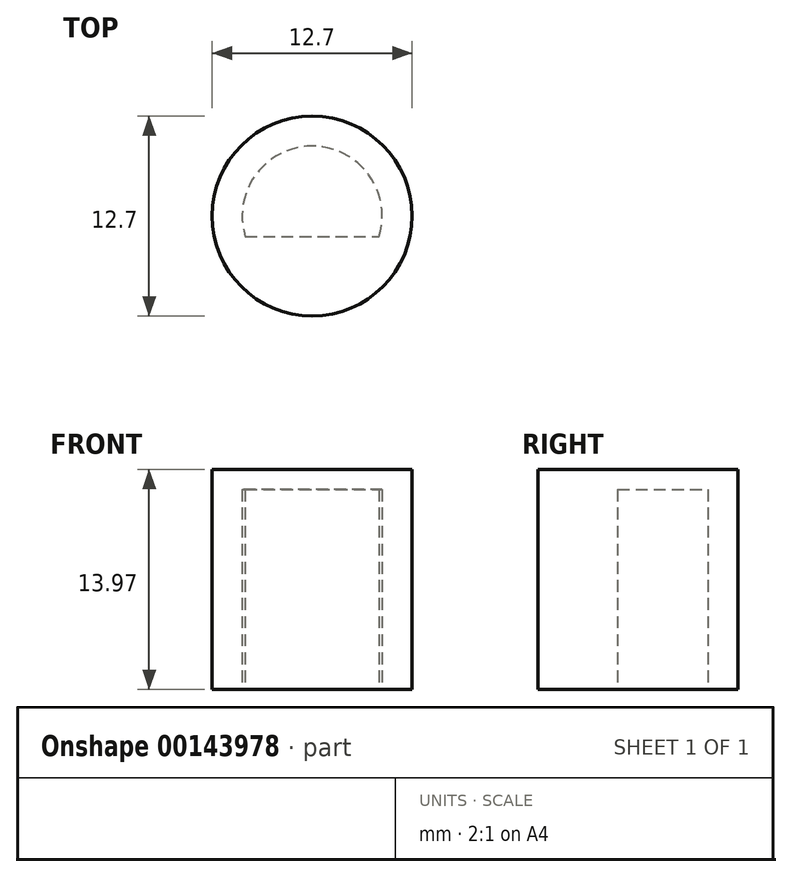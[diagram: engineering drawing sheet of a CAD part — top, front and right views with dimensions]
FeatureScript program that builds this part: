
annotation { "Feature Type Name" : "Feature", "Feature Type Description" : "" }
export const myFeature = defineFeature(function(context is Context, id is Id, definition is map)
    precondition{}
    {
        {
            var Q0;
            Q0=qCreatedBy(makeId("Top.planeOp"),FACE);
            var sketch = newSketch(context, id + "F0", { "sketchPlane" : qUnion([Q0])});
            skPoint(sketch, "E0", {"position": v(0, 0.13) * mm});
            skPoint(sketch, "E1", {"position": v(0, 4.45) * mm});
            skCircle(sketch, "E2", {"center": v(0, 0) * mm, "radius": 6.35 * mm});
            skArc(sketch, "E3", {"start": v(4.25, -1.3) * mm, "mid": v(0, 4.45) * mm, "end": v(-4.25, -1.3) * mm});
            skLineSegment(sketch, "E4", {"start": v(-4.25, -1.3) * mm, "end": v(4.25, -1.3) * mm});
            skSolve(sketch);
        }
        {
            var Q0;
            Q0=makeQuery(id+"F0.imprint","IMPRINT",FACE,{"disambiguationData":[TD([[makeQuery(id+"F0.imprint","IMPRINT",EDGE,{"derivedFrom":sQuery(id+"F0.wireOp",EDGE,"s4ZK6kcC-YwtM-Ympy-6Isc-HiUL8Dsxxq34")}),-1.0]])]});
            var Q1;
            Q1=makeQuery(id+"F0.imprint","IMPRINT",FACE,{"disambiguationData":[TD([[makeQuery(id+"F0.imprint","IMPRINT",EDGE,{"derivedFrom":sQuery(id+"F0.wireOp",EDGE,"E2")}),1.0]])]});
            extrude(context, id + "F1", {"entities" : qUnion([Q0, Q1]), "depth" : 12.7 * mm});
        }
        {
            var Q0;
            Q0=makeQuery(id+"F1.opExtrude","CAP_FACE",FACE,{"disambiguationData":[OSD([sQuery(id+"F0.wireOp",EDGE,"s4ZK6kcC-YwtM-Ympy-6Isc-HiUL8Dsxxq34"),sQuery(id+"F0.wireOp",EDGE,"buqjDm1d-5vtQ-84jR-WtLd-hSESKNRjcbsC"),sQuery(id+"F0.wireOp",EDGE,"E2")])],"isStart":false});
            cPlane(context, id + "F2", {"entities" : qUnion([Q0]), "cplaneType" : CPlaneType.OFFSET, "offset" : 0 * mm, "width" : 152.4 * mm, "height" : 152.4 * mm});
        }
        {
            var Q0;
            Q0=qCreatedBy(id+"F2.planeOp",FACE);
            var sketch = newSketch(context, id + "F3", { "sketchPlane" : qUnion([Q0])});
            skCircle(sketch, "E5", {"center": v(0, 0) * mm, "radius": 6.35 * mm});
            skSolve(sketch);
        }
        {
            var Q0;
            Q0=makeQuery(id+"F3.imprint","IMPRINT",FACE,{"disambiguationData":[TD([[makeQuery(id+"F3.imprint","IMPRINT",EDGE,{"derivedFrom":sQuery(id+"F3.wireOp",EDGE,"E5")}),1.0]])]});
            extrude(context, id + "F4", {"entities" : qUnion([Q0]), "operationType" : NewBodyOperationType.ADD, "depth" : 1.27 * mm});
        }
    });
